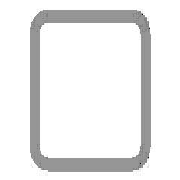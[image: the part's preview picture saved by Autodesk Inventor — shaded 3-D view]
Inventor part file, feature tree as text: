
AUTODESK INVENTOR PART (.ipt)
format: ipt  version: 2025 (Build 290162010, 162A)  size: 133,632 bytes
history: native  units: mm (DEFAULTED — no unit token found)
features: other x4, sketch x1, plane x1
ambient origin geometry x8: Origin, YZ Plane, XZ Plane, XY Plane, X Axis, Y Axis, Z Axis, Center Point
bodies: Solid1 (feature_tree), Body (feature_tree)
feature tree (6):
  parser-record x1  (decoder bookkeeping rows leaked as tree rows — omitted from the tree; the rows remain in map.json)
  other  "Driven Length"
  other  "Start Plane"
  other  "End Plane"
  sketch  "Sketch3"  dims[d3=500.0mm d4=0.0mm d7=8.0mm d9=50.0mm d11=50.0mm d12=4.0mm d13=-0.0mm d14=500.0mm d15=25.0mm d16=25.0mm d17=90.0deg d18=500.0mm]
  plane  "Work Plane3"
